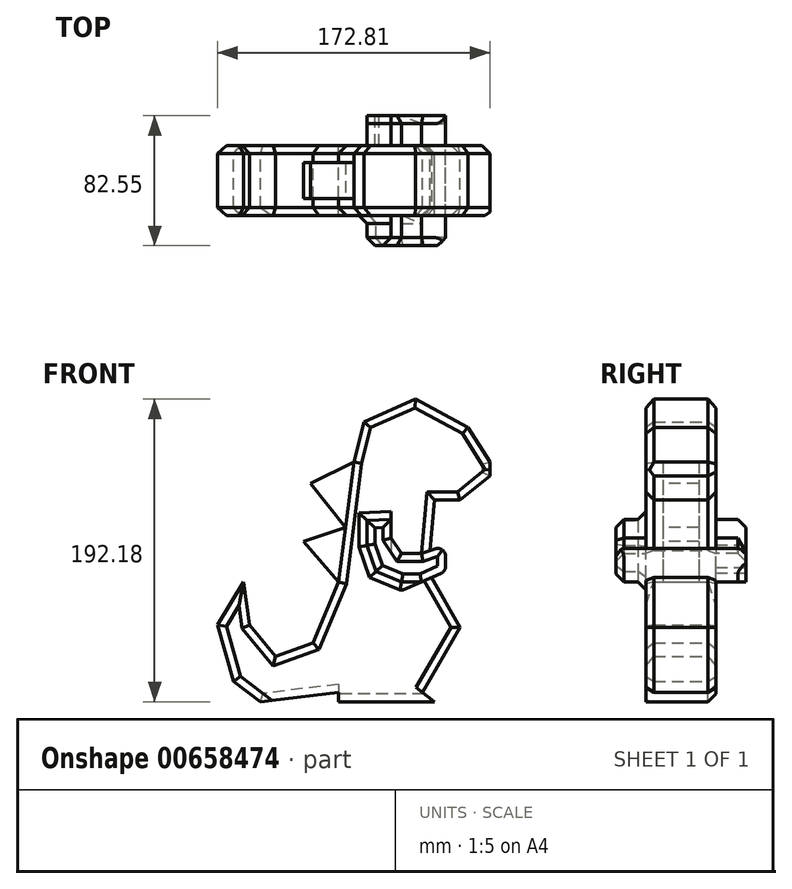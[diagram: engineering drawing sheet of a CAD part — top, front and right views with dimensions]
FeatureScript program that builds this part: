
annotation { "Feature Type Name" : "Feature", "Feature Type Description" : "" }
export const myFeature = defineFeature(function(context is Context, id is Id, definition is map)
    precondition{}
    {
        {
            var Q0;
            Q0=qCreatedBy(makeId("Front.planeOp"),FACE);
            var sketch = newSketch(context, id + "F0", { "sketchPlane" : qUnion([Q0])});
            skLineSegment(sketch, "E0", {"start": v(77.08, 51.94) * mm, "end": v(77.08, 55.91) * mm});
            skLineSegment(sketch, "E1", {"start": v(-60.47, 0) * mm, "end": v(-76.86, -27.51) * mm});
            skLineSegment(sketch, "E2", {"start": v(-76.86, -27.51) * mm, "end": v(-66.68, -63.13) * mm});
            skLineSegment(sketch, "E3", {"start": v(-60.47, 0) * mm, "end": v(-56.5, -27.51) * mm});
            skLineSegment(sketch, "E4", {"start": v(-56.5, -27.51) * mm, "end": v(-40.11, -47.38) * mm});
            skLineSegment(sketch, "E5", {"start": v(-40.11, -47.38) * mm, "end": v(-16.28, -38.93) * mm});
            skLineSegment(sketch, "E6", {"start": v(-16.28, -38.93) * mm, "end": v(0, 0) * mm});
            skPoint(sketch, "E7.start.orphan", {"position": v(68.14, 60.88) * mm});
            skPoint(sketch, "E8.end.orphan", {"position": v(45.3, 0) * mm});
            skPoint(sketch, "E8.start.orphan", {"position": v(68.14, 10.23) * mm});
            skPoint(sketch, "E9.end.orphan", {"position": v(38.54, 76.27) * mm});
            skLineSegment(sketch, "E10", {"start": v(0, 0) * mm, "end": v(9.55, 76.27) * mm});
            skLineSegment(sketch, "E11", {"start": v(-49.55, -76.18) * mm, "end": v(-66.68, -63.13) * mm});
            skLineSegment(sketch, "E12", {"start": v(-49.55, -76.18) * mm, "end": v(0, -70.22) * mm});
            skLineSegment(sketch, "E13", {"start": v(0, -70.22) * mm, "end": v(0, -76.18) * mm});
            skLineSegment(sketch, "E14", {"start": v(0, -76.18) * mm, "end": v(60.7, -76.18) * mm});
            skLineSegment(sketch, "E15", {"start": v(60.7, -76.18) * mm, "end": v(53.24, -70.22) * mm});
            skLineSegment(sketch, "E16", {"start": v(53.24, -70.22) * mm, "end": v(77.08, -29) * mm});
            skLineSegment(sketch, "E17", {"start": v(77.08, -29) * mm, "end": v(56.72, 6.75) * mm});
            skLineSegment(sketch, "E18", {"start": v(56.72, 6.75) * mm, "end": v(60.7, 51.94) * mm});
            skLineSegment(sketch, "E19", {"start": v(60.7, 51.94) * mm, "end": v(77.08, 51.94) * mm});
            skPoint(sketch, "E19.endSnap0", {"position": v(77.08, 55.91) * mm});
            skLineSegment(sketch, "E20", {"start": v(77.08, 51.94) * mm, "end": v(95.95, 67.33) * mm});
            skLineSegment(sketch, "E21", {"start": v(95.95, 67.33) * mm, "end": v(95.95, 76.27) * mm});
            skLineSegment(sketch, "E22", {"start": v(95.95, 76.27) * mm, "end": v(82.05, 98.12) * mm});
            skLineSegment(sketch, "E23", {"start": v(82.05, 98.12) * mm, "end": v(48.78, 116) * mm});
            skLineSegment(sketch, "E24", {"start": v(48.78, 116) * mm, "end": v(16, 101.6) * mm});
            skLineSegment(sketch, "E25", {"start": v(16, 101.6) * mm, "end": v(9.55, 76.27) * mm});
            skPoint(sketch, "E26.orphan", {"position": v(77.08, 76.27) * mm});
            skPoint(sketch, "E27.orphan", {"position": v(77.08, 35.55) * mm});
            skPoint(sketch, "E28.end.orphan", {"position": v(0, 76.27) * mm});
            skSolve(sketch);
        }
        {
            var Q0;
            Q0=makeQuery(id+"F0.imprint","IMPRINT",FACE,{"disambiguationData":[TD([[makeQuery(id+"F0.imprint","IMPRINT",EDGE,{"derivedFrom":sQuery(id+"F0.wireOp",EDGE,"E1")}),1.0]])]});
            extrude(context, id + "F1", {"entities" : qUnion([Q0]), "depth" : 44.45 * mm, "offsetDistance" : 25.4 * mm});
        }
        {
            var Q0;
            Q0=makeQuery(id+"F1.opExtrude","CAP_EDGE",EDGE,{"disambiguationData":[OSD([sQuery(id+"F0.wireOp",EDGE,"E24")])],"isStart":false});
            var Q1;
            Q1=makeQuery(id+"F1.opExtrude","CAP_EDGE",EDGE,{"disambiguationData":[OSD([sQuery(id+"F0.wireOp",EDGE,"E23")])],"isStart":false});
            var Q2;
            Q2=makeQuery(id+"F1.opExtrude","CAP_EDGE",EDGE,{"disambiguationData":[OSD([sQuery(id+"F0.wireOp",EDGE,"E22")])],"isStart":false});
            var Q3;
            Q3=makeQuery(id+"F1.opExtrude","CAP_EDGE",EDGE,{"disambiguationData":[OSD([sQuery(id+"F0.wireOp",EDGE,"E20")])],"isStart":false});
            var Q4;
            Q4=makeQuery(id+"F1.opExtrude","CAP_EDGE",EDGE,{"disambiguationData":[OSD([sQuery(id+"F0.wireOp",EDGE,"E19")])],"isStart":false});
            var Q5;
            Q5=makeQuery(id+"F1.opExtrude","CAP_EDGE",EDGE,{"disambiguationData":[OSD([sQuery(id+"F0.wireOp",EDGE,"E18")])],"isStart":false});
            var Q6;
            Q6=makeQuery(id+"F1.opExtrude","CAP_EDGE",EDGE,{"disambiguationData":[OSD([sQuery(id+"F0.wireOp",EDGE,"E17")])],"isStart":false});
            var Q7;
            Q7=makeQuery(id+"F1.opExtrude","CAP_EDGE",EDGE,{"disambiguationData":[OSD([sQuery(id+"F0.wireOp",EDGE,"E16")])],"isStart":false});
            var Q8;
            Q8=makeQuery(id+"F1.opExtrude","CAP_EDGE",EDGE,{"disambiguationData":[OSD([sQuery(id+"F0.wireOp",EDGE,"E10")])],"isStart":false});
            var Q9;
            Q9=makeQuery(id+"F1.opExtrude","CAP_EDGE",EDGE,{"disambiguationData":[OSD([sQuery(id+"F0.wireOp",EDGE,"E6")])],"isStart":false});
            var Q10;
            Q10=makeQuery(id+"F1.opExtrude","CAP_EDGE",EDGE,{"disambiguationData":[OSD([sQuery(id+"F0.wireOp",EDGE,"E25")])],"isStart":false});
            var Q11;
            Q11=makeQuery(id+"F1.opExtrude","CAP_EDGE",EDGE,{"disambiguationData":[OSD([sQuery(id+"F0.wireOp",EDGE,"E5")])],"isStart":false});
            var Q12;
            Q12=makeQuery(id+"F1.opExtrude","CAP_EDGE",EDGE,{"disambiguationData":[OSD([sQuery(id+"F0.wireOp",EDGE,"E4")])],"isStart":false});
            var Q13;
            Q13=makeQuery(id+"F1.opExtrude","CAP_EDGE",EDGE,{"disambiguationData":[OSD([sQuery(id+"F0.wireOp",EDGE,"E3")])],"isStart":false});
            var Q14;
            Q14=makeQuery(id+"F1.opExtrude","CAP_EDGE",EDGE,{"disambiguationData":[OSD([sQuery(id+"F0.wireOp",EDGE,"E1")])],"isStart":false});
            var Q15;
            Q15=makeQuery(id+"F1.opExtrude","CAP_EDGE",EDGE,{"disambiguationData":[OSD([sQuery(id+"F0.wireOp",EDGE,"E2")])],"isStart":false});
            var Q16;
            Q16=makeQuery(id+"F1.opExtrude","CAP_EDGE",EDGE,{"disambiguationData":[OSD([sQuery(id+"F0.wireOp",EDGE,"E11")])],"isStart":false});
            var Q17;
            Q17=makeQuery(id+"F1.opExtrude","CAP_EDGE",EDGE,{"disambiguationData":[OSD([sQuery(id+"F0.wireOp",EDGE,"E24")])],"isStart":true});
            var Q18;
            Q18=makeQuery(id+"F1.opExtrude","CAP_EDGE",EDGE,{"disambiguationData":[OSD([sQuery(id+"F0.wireOp",EDGE,"E23")])],"isStart":true});
            var Q19;
            Q19=makeQuery(id+"F1.opExtrude","CAP_EDGE",EDGE,{"disambiguationData":[OSD([sQuery(id+"F0.wireOp",EDGE,"E22")])],"isStart":true});
            var Q20;
            Q20=makeQuery(id+"F1.opExtrude","CAP_EDGE",EDGE,{"disambiguationData":[OSD([sQuery(id+"F0.wireOp",EDGE,"E21")])],"isStart":true});
            var Q21;
            Q21=makeQuery(id+"F1.opExtrude","CAP_EDGE",EDGE,{"disambiguationData":[OSD([sQuery(id+"F0.wireOp",EDGE,"E20")])],"isStart":true});
            var Q22;
            Q22=makeQuery(id+"F1.opExtrude","CAP_EDGE",EDGE,{"disambiguationData":[OSD([sQuery(id+"F0.wireOp",EDGE,"E19")])],"isStart":true});
            var Q23;
            Q23=makeQuery(id+"F1.opExtrude","CAP_EDGE",EDGE,{"disambiguationData":[OSD([sQuery(id+"F0.wireOp",EDGE,"E18")])],"isStart":true});
            var Q24;
            Q24=makeQuery(id+"F1.opExtrude","CAP_EDGE",EDGE,{"disambiguationData":[OSD([sQuery(id+"F0.wireOp",EDGE,"E17")])],"isStart":true});
            var Q25;
            Q25=makeQuery(id+"F1.opExtrude","CAP_EDGE",EDGE,{"disambiguationData":[OSD([sQuery(id+"F0.wireOp",EDGE,"E16")])],"isStart":true});
            var Q26;
            Q26=makeQuery(id+"F1.opExtrude","CAP_EDGE",EDGE,{"disambiguationData":[OSD([sQuery(id+"F0.wireOp",EDGE,"E14")])],"isStart":true});
            var Q27;
            Q27=makeQuery(id+"F1.opExtrude","CAP_EDGE",EDGE,{"disambiguationData":[OSD([sQuery(id+"F0.wireOp",EDGE,"E25")])],"isStart":true});
            var Q28;
            Q28=makeQuery(id+"F1.opExtrude","CAP_EDGE",EDGE,{"disambiguationData":[OSD([sQuery(id+"F0.wireOp",EDGE,"E10")])],"isStart":true});
            var Q29;
            Q29=makeQuery(id+"F1.opExtrude","CAP_EDGE",EDGE,{"disambiguationData":[OSD([sQuery(id+"F0.wireOp",EDGE,"E6")])],"isStart":true});
            var Q30;
            Q30=makeQuery(id+"F1.opExtrude","CAP_EDGE",EDGE,{"disambiguationData":[OSD([sQuery(id+"F0.wireOp",EDGE,"E5")])],"isStart":true});
            var Q31;
            Q31=makeQuery(id+"F1.opExtrude","CAP_EDGE",EDGE,{"disambiguationData":[OSD([sQuery(id+"F0.wireOp",EDGE,"E4")])],"isStart":true});
            var Q32;
            Q32=makeQuery(id+"F1.opExtrude","CAP_EDGE",EDGE,{"disambiguationData":[OSD([sQuery(id+"F0.wireOp",EDGE,"E3")])],"isStart":true});
            var Q33;
            Q33=makeQuery(id+"F1.opExtrude","CAP_EDGE",EDGE,{"disambiguationData":[OSD([sQuery(id+"F0.wireOp",EDGE,"E1")])],"isStart":true});
            var Q34;
            Q34=makeQuery(id+"F1.opExtrude","CAP_EDGE",EDGE,{"disambiguationData":[OSD([sQuery(id+"F0.wireOp",EDGE,"E2")])],"isStart":true});
            var Q35;
            Q35=makeQuery(id+"F1.opExtrude","CAP_EDGE",EDGE,{"disambiguationData":[OSD([sQuery(id+"F0.wireOp",EDGE,"E11")])],"isStart":true});
            var Q36;
            Q36=makeQuery(id+"F1.opExtrude","CAP_EDGE",EDGE,{"disambiguationData":[OSD([sQuery(id+"F0.wireOp",EDGE,"E12")])],"isStart":true});
            chamfer(context, id + "F2", {"entities" : qUnion([Q0, Q1, Q2, Q3, Q4, Q5, Q6, Q7, Q8, Q9, Q10, Q11, Q12, Q13, Q14, Q15, Q16, Q17, Q18, Q19, Q20, Q21, Q22, Q23, Q24, Q25, Q26, Q27, Q28, Q29, Q30, Q31, Q32, Q33, Q34, Q35, Q36]), "width" : 5.08 * mm, "tangentPropagation" : true});
        }
        {
            var Q0;
            Q0=makeQuery(id+"F1.opExtrude","CAP_FACE",FACE,{"disambiguationData":[OSD([sQuery(id+"F0.wireOp",EDGE,"E1"),sQuery(id+"F0.wireOp",EDGE,"E2"),sQuery(id+"F0.wireOp",EDGE,"E3"),sQuery(id+"F0.wireOp",EDGE,"E4"),sQuery(id+"F0.wireOp",EDGE,"E5"),sQuery(id+"F0.wireOp",EDGE,"E6"),sQuery(id+"F0.wireOp",EDGE,"E10"),sQuery(id+"F0.wireOp",EDGE,"E11"),sQuery(id+"F0.wireOp",EDGE,"E12"),sQuery(id+"F0.wireOp",EDGE,"E13"),sQuery(id+"F0.wireOp",EDGE,"E14"),sQuery(id+"F0.wireOp",EDGE,"E15"),sQuery(id+"F0.wireOp",EDGE,"E16"),sQuery(id+"F0.wireOp",EDGE,"E17"),sQuery(id+"F0.wireOp",EDGE,"E18"),sQuery(id+"F0.wireOp",EDGE,"E19"),sQuery(id+"F0.wireOp",EDGE,"E20"),sQuery(id+"F0.wireOp",EDGE,"E21"),sQuery(id+"F0.wireOp",EDGE,"E22"),sQuery(id+"F0.wireOp",EDGE,"E23"),sQuery(id+"F0.wireOp",EDGE,"E24"),sQuery(id+"F0.wireOp",EDGE,"E25")])],"isStart":true});
            var sketch = newSketch(context, id + "F3", { "sketchPlane" : qUnion([Q0])});
            skLineSegment(sketch, "E29", {"start": v(-33.23, 39.73) * mm, "end": v(-33.23, 27.8) * mm});
            skLineSegment(sketch, "E30", {"start": v(-33.23, 27.8) * mm, "end": v(-39.78, 18.16) * mm});
            skLineSegment(sketch, "E31", {"start": v(-39.78, 18.16) * mm, "end": v(-52.62, 18.16) * mm});
            skLineSegment(sketch, "E32", {"start": v(-52.62, 18.16) * mm, "end": v(-67.9, 23.17) * mm});
            skLineSegment(sketch, "E33", {"start": v(-67.9, 23.17) * mm, "end": v(-67.9, 6.61) * mm});
            skLineSegment(sketch, "E34", {"start": v(-67.9, 6.61) * mm, "end": v(-52.62, 0) * mm});
            skLineSegment(sketch, "E35", {"start": v(-52.62, 0) * mm, "end": v(-39.78, 0) * mm});
            skLineSegment(sketch, "E36", {"start": v(-39.78, 0) * mm, "end": v(-23.6, 6.61) * mm});
            skLineSegment(sketch, "E37", {"start": v(-23.6, 6.61) * mm, "end": v(-17.83, 23.17) * mm});
            skLineSegment(sketch, "E38", {"start": v(-17.83, 23.17) * mm, "end": v(-17.83, 38.96) * mm});
            skLineSegment(sketch, "E39", {"start": v(-17.83, 38.96) * mm, "end": v(-33.23, 39.73) * mm});
            skSolve(sketch);
        }
        {
            var Q0;
            {var subQ9=sQuery(id+"F3.wireOp",EDGE,"E32");Q0=makeQuery(id+"F3.imprint","IMPRINT",FACE,{"disambiguationData":[TD([[makeQuery(id+"F3.imprint","IMPRINT",EDGE,{"derivedFrom":subQ9}),1.0]])]});}
            var Q1;
            Q1=makeQuery(id+"F3.imprint","IMPRINT",FACE,{"disambiguationData":[TD([[makeQuery(id+"F3.imprint","IMPRINT",EDGE,{"derivedFrom":sQuery(id+"F3.wireOp",EDGE,"E29")}),1.0]])]});
            extrude(context, id + "F4", {"entities" : qUnion([Q0, Q1]), "operationType" : NewBodyOperationType.ADD, "oppositeDirection" : true, "depth" : 63.5 * mm, "offsetDistance" : 25.4 * mm});
        }
        {
            var Q0;
            Q0 = qSketchRegion(id + "F3", true);
            extrude(context, id + "F5", {"entities" : qUnion([Q0]), "operationType" : NewBodyOperationType.ADD, "depth" : 19.05 * mm, "offsetDistance" : 25.4 * mm});
        }
        {
            var Q0;
            Q0=makeQuery(id+"F5.opExtrude","CAP_EDGE",EDGE,{"disambiguationData":[OSD([sQuery(id+"F3.wireOp",EDGE,"E39")])],"isStart":true});
            var Q1;
            Q1=makeQuery(id+"F5.opExtrude","CAP_EDGE",EDGE,{"disambiguationData":[OSD([sQuery(id+"F3.wireOp",EDGE,"E39")])],"isStart":false});
            var Q2;
            Q2=makeQuery(id+"F5.opExtrude","CAP_EDGE",EDGE,{"disambiguationData":[OSD([sQuery(id+"F3.wireOp",EDGE,"E32")])],"isStart":false});
            var Q3;
            Q3=makeQuery(id+"F5.opExtrude","CAP_EDGE",EDGE,{"disambiguationData":[OSD([sQuery(id+"F3.wireOp",EDGE,"E31")])],"isStart":false});
            var Q4;
            Q4=makeQuery(id+"F5.opExtrude","CAP_EDGE",EDGE,{"disambiguationData":[OSD([sQuery(id+"F3.wireOp",EDGE,"E30")])],"isStart":false});
            var Q5;
            Q5=makeQuery(id+"F5.opExtrude","CAP_EDGE",EDGE,{"disambiguationData":[OSD([sQuery(id+"F3.wireOp",EDGE,"E38")])],"isStart":true});
            var Q6;
            Q6=makeQuery(id+"F5.opExtrude","CAP_EDGE",EDGE,{"disambiguationData":[OSD([sQuery(id+"F3.wireOp",EDGE,"E37")])],"isStart":true});
            var Q7;
            Q7=makeQuery(id+"F5.opExtrude","SWEPT_EDGE",EDGE,{"disambiguationData":[OSD([sQuery(id+"F3.wireOp",EDGE,"E36"),sQuery(id+"F3.wireOp",EDGE,"E37")])]});
            var Q8;
            Q8=makeQuery(id+"F5.opExtrude","CAP_EDGE",EDGE,{"disambiguationData":[OSD([sQuery(id+"F3.wireOp",EDGE,"E35")])],"isStart":true});
            var Q9;
            Q9=makeQuery(id+"F5.opExtrude","CAP_EDGE",EDGE,{"disambiguationData":[OSD([sQuery(id+"F3.wireOp",EDGE,"E34")])],"isStart":false});
            var Q10;
            Q10=makeQuery(id+"F4.boolean.opBoolean","INTERSECT",EDGE,{"derivedFrom":[makeQuery(id+"F1.opExtrude","CAP_FACE",FACE,{"disambiguationData":[OSD([sQuery(id+"F0.wireOp",EDGE,"E1"),sQuery(id+"F0.wireOp",EDGE,"E2"),sQuery(id+"F0.wireOp",EDGE,"E3"),sQuery(id+"F0.wireOp",EDGE,"E4"),sQuery(id+"F0.wireOp",EDGE,"E5"),sQuery(id+"F0.wireOp",EDGE,"E6"),sQuery(id+"F0.wireOp",EDGE,"E10"),sQuery(id+"F0.wireOp",EDGE,"E11"),sQuery(id+"F0.wireOp",EDGE,"E12"),sQuery(id+"F0.wireOp",EDGE,"E13"),sQuery(id+"F0.wireOp",EDGE,"E14"),sQuery(id+"F0.wireOp",EDGE,"E15"),sQuery(id+"F0.wireOp",EDGE,"E16"),sQuery(id+"F0.wireOp",EDGE,"E17"),sQuery(id+"F0.wireOp",EDGE,"E18"),sQuery(id+"F0.wireOp",EDGE,"E19"),sQuery(id+"F0.wireOp",EDGE,"E20"),sQuery(id+"F0.wireOp",EDGE,"E21"),sQuery(id+"F0.wireOp",EDGE,"E22"),sQuery(id+"F0.wireOp",EDGE,"E23"),sQuery(id+"F0.wireOp",EDGE,"E24"),sQuery(id+"F0.wireOp",EDGE,"E25")])],"isStart":false}),makeQuery(id+"F4.opExtrude","SWEPT_FACE",FACE,{"disambiguationData":[OSD([sQuery(id+"F3.wireOp",EDGE,"E39")])]})]});
            var Q11;
            Q11=makeQuery(id+"F4.opExtrude","CAP_EDGE",EDGE,{"disambiguationData":[OSD([sQuery(id+"F3.wireOp",EDGE,"E39")])],"isStart":false});
            var Q12;
            Q12=makeQuery(id+"F4.opExtrude","CAP_EDGE",EDGE,{"disambiguationData":[OSD([sQuery(id+"F3.wireOp",EDGE,"E29")])],"isStart":false});
            var Q13;
            Q13=makeQuery(id+"F4.opExtrude","CAP_EDGE",EDGE,{"disambiguationData":[OSD([sQuery(id+"F3.wireOp",EDGE,"E30")])],"isStart":false});
            var Q14;
            Q14=makeQuery(id+"F4.opExtrude","CAP_EDGE",EDGE,{"disambiguationData":[OSD([sQuery(id+"F3.wireOp",EDGE,"E31")])],"isStart":false});
            var Q15;
            Q15=makeQuery(id+"F4.opExtrude","CAP_EDGE",EDGE,{"disambiguationData":[OSD([sQuery(id+"F3.wireOp",EDGE,"E32")])],"isStart":false});
            var Q16;
            Q16=makeQuery(id+"F4.boolean.opBoolean","INTERSECT",EDGE,{"derivedFrom":[makeQuery(id+"F1.opExtrude","CAP_FACE",FACE,{"disambiguationData":[OSD([sQuery(id+"F0.wireOp",EDGE,"E1"),sQuery(id+"F0.wireOp",EDGE,"E2"),sQuery(id+"F0.wireOp",EDGE,"E3"),sQuery(id+"F0.wireOp",EDGE,"E4"),sQuery(id+"F0.wireOp",EDGE,"E5"),sQuery(id+"F0.wireOp",EDGE,"E6"),sQuery(id+"F0.wireOp",EDGE,"E10"),sQuery(id+"F0.wireOp",EDGE,"E11"),sQuery(id+"F0.wireOp",EDGE,"E12"),sQuery(id+"F0.wireOp",EDGE,"E13"),sQuery(id+"F0.wireOp",EDGE,"E14"),sQuery(id+"F0.wireOp",EDGE,"E15"),sQuery(id+"F0.wireOp",EDGE,"E16"),sQuery(id+"F0.wireOp",EDGE,"E17"),sQuery(id+"F0.wireOp",EDGE,"E18"),sQuery(id+"F0.wireOp",EDGE,"E19"),sQuery(id+"F0.wireOp",EDGE,"E20"),sQuery(id+"F0.wireOp",EDGE,"E21"),sQuery(id+"F0.wireOp",EDGE,"E22"),sQuery(id+"F0.wireOp",EDGE,"E23"),sQuery(id+"F0.wireOp",EDGE,"E24"),sQuery(id+"F0.wireOp",EDGE,"E25")])],"isStart":false}),makeQuery(id+"F4.opExtrude","SWEPT_FACE",FACE,{"disambiguationData":[OSD([sQuery(id+"F3.wireOp",EDGE,"E35")])]})]});
            var Q17;
            Q17=makeQuery(id+"F4.boolean.opBoolean","INTERSECT",EDGE,{"derivedFrom":[makeQuery(id+"F1.opExtrude","CAP_FACE",FACE,{"disambiguationData":[OSD([sQuery(id+"F0.wireOp",EDGE,"E1"),sQuery(id+"F0.wireOp",EDGE,"E2"),sQuery(id+"F0.wireOp",EDGE,"E3"),sQuery(id+"F0.wireOp",EDGE,"E4"),sQuery(id+"F0.wireOp",EDGE,"E5"),sQuery(id+"F0.wireOp",EDGE,"E6"),sQuery(id+"F0.wireOp",EDGE,"E10"),sQuery(id+"F0.wireOp",EDGE,"E11"),sQuery(id+"F0.wireOp",EDGE,"E12"),sQuery(id+"F0.wireOp",EDGE,"E13"),sQuery(id+"F0.wireOp",EDGE,"E14"),sQuery(id+"F0.wireOp",EDGE,"E15"),sQuery(id+"F0.wireOp",EDGE,"E16"),sQuery(id+"F0.wireOp",EDGE,"E17"),sQuery(id+"F0.wireOp",EDGE,"E18"),sQuery(id+"F0.wireOp",EDGE,"E19"),sQuery(id+"F0.wireOp",EDGE,"E20"),sQuery(id+"F0.wireOp",EDGE,"E21"),sQuery(id+"F0.wireOp",EDGE,"E22"),sQuery(id+"F0.wireOp",EDGE,"E23"),sQuery(id+"F0.wireOp",EDGE,"E24"),sQuery(id+"F0.wireOp",EDGE,"E25")])],"isStart":false}),makeQuery(id+"F4.opExtrude","SWEPT_FACE",FACE,{"disambiguationData":[OSD([sQuery(id+"F3.wireOp",EDGE,"E36")])]})]});
            var Q18;
            Q18=makeQuery(id+"F4.boolean.opBoolean","INTERSECT",EDGE,{"derivedFrom":[makeQuery(id+"F1.opExtrude","CAP_FACE",FACE,{"disambiguationData":[OSD([sQuery(id+"F0.wireOp",EDGE,"E1"),sQuery(id+"F0.wireOp",EDGE,"E2"),sQuery(id+"F0.wireOp",EDGE,"E3"),sQuery(id+"F0.wireOp",EDGE,"E4"),sQuery(id+"F0.wireOp",EDGE,"E5"),sQuery(id+"F0.wireOp",EDGE,"E6"),sQuery(id+"F0.wireOp",EDGE,"E10"),sQuery(id+"F0.wireOp",EDGE,"E11"),sQuery(id+"F0.wireOp",EDGE,"E12"),sQuery(id+"F0.wireOp",EDGE,"E13"),sQuery(id+"F0.wireOp",EDGE,"E14"),sQuery(id+"F0.wireOp",EDGE,"E15"),sQuery(id+"F0.wireOp",EDGE,"E16"),sQuery(id+"F0.wireOp",EDGE,"E17"),sQuery(id+"F0.wireOp",EDGE,"E18"),sQuery(id+"F0.wireOp",EDGE,"E19"),sQuery(id+"F0.wireOp",EDGE,"E20"),sQuery(id+"F0.wireOp",EDGE,"E21"),sQuery(id+"F0.wireOp",EDGE,"E22"),sQuery(id+"F0.wireOp",EDGE,"E23"),sQuery(id+"F0.wireOp",EDGE,"E24"),sQuery(id+"F0.wireOp",EDGE,"E25")])],"isStart":false}),makeQuery(id+"F4.opExtrude","SWEPT_FACE",FACE,{"disambiguationData":[OSD([sQuery(id+"F3.wireOp",EDGE,"E38")])]})]});
            var Q19;
            Q19=makeQuery(id+"F4.boolean.opBoolean","INTERSECT",EDGE,{"derivedFrom":[makeQuery(id+"F1.opExtrude","CAP_FACE",FACE,{"disambiguationData":[OSD([sQuery(id+"F0.wireOp",EDGE,"E1"),sQuery(id+"F0.wireOp",EDGE,"E2"),sQuery(id+"F0.wireOp",EDGE,"E3"),sQuery(id+"F0.wireOp",EDGE,"E4"),sQuery(id+"F0.wireOp",EDGE,"E5"),sQuery(id+"F0.wireOp",EDGE,"E6"),sQuery(id+"F0.wireOp",EDGE,"E10"),sQuery(id+"F0.wireOp",EDGE,"E11"),sQuery(id+"F0.wireOp",EDGE,"E12"),sQuery(id+"F0.wireOp",EDGE,"E13"),sQuery(id+"F0.wireOp",EDGE,"E14"),sQuery(id+"F0.wireOp",EDGE,"E15"),sQuery(id+"F0.wireOp",EDGE,"E16"),sQuery(id+"F0.wireOp",EDGE,"E17"),sQuery(id+"F0.wireOp",EDGE,"E18"),sQuery(id+"F0.wireOp",EDGE,"E19"),sQuery(id+"F0.wireOp",EDGE,"E20"),sQuery(id+"F0.wireOp",EDGE,"E21"),sQuery(id+"F0.wireOp",EDGE,"E22"),sQuery(id+"F0.wireOp",EDGE,"E23"),sQuery(id+"F0.wireOp",EDGE,"E24"),sQuery(id+"F0.wireOp",EDGE,"E25")])],"isStart":false}),makeQuery(id+"F4.opExtrude","SWEPT_FACE",FACE,{"disambiguationData":[OSD([sQuery(id+"F3.wireOp",EDGE,"E37")])]})]});
            chamfer(context, id + "F6", {"entities" : qUnion([Q0, Q1, Q2, Q3, Q4, Q5, Q6, Q7, Q8, Q9, Q10, Q11, Q12, Q13, Q14, Q15, Q16, Q17, Q18, Q19]), "width" : 5.08 * mm, "tangentPropagation" : true});
        }
        {
            var Q0;
            Q0=makeQuery(id+"F1.opExtrude","SWEPT_FACE",FACE,{"disambiguationData":[OSD([sQuery(id+"F0.wireOp",EDGE,"E10")])]});
            var sketch = newSketch(context, id + "F7", { "sketchPlane" : qUnion([Q0])});
            skLineSegment(sketch, "E40.bottom", {"start": v(17.14, 76.86) * mm, "end": v(26.38, 76.86) * mm});
            skLineSegment(sketch, "E40.top", {"start": v(17.14, 0) * mm, "end": v(26.38, 0) * mm});
            skLineSegment(sketch, "E40.left", {"start": v(17.14, 76.86) * mm, "end": v(17.14, 0) * mm});
            skLineSegment(sketch, "E40.right", {"start": v(26.38, 76.86) * mm, "end": v(26.38, 0) * mm});
            skSolve(sketch);
        }
        {
            var Q0;
            Q0 = qSketchRegion(id + "F7", true);
            extrude(context, id + "F8", {"entities" : qUnion([Q0]), "operationType" : NewBodyOperationType.ADD, "depth" : 25.4 * mm, "offsetDistance" : 25.4 * mm});
        }
        {
            var Q0;
            Q0=makeQuery(id+"F8.opExtrude","SWEPT_FACE",FACE,{"disambiguationData":[OSD([sQuery(id+"F7.wireOp",EDGE,"E40.left")])]});
            var sketch = newSketch(context, id + "F9", { "sketchPlane" : qUnion([Q0])});
            skLineSegment(sketch, "E41", {"start": v(-9.55, 76.27) * mm, "end": v(17.76, 62.62) * mm});
            skLineSegment(sketch, "E42", {"start": v(17.76, 62.62) * mm, "end": v(-4.33, 34.58) * mm});
            skLineSegment(sketch, "E43", {"start": v(-4.33, 34.58) * mm, "end": v(22.4, 25.6) * mm});
            skLineSegment(sketch, "E44", {"start": v(22.4, 25.6) * mm, "end": v(0, 0) * mm});
            skSolve(sketch);
        }
        {
            var Q0;
            {var subQ0=sQuery(id+"F9.wireOp",EDGE,"E41");Q0=makeQuery(id+"F9.imprint","IMPRINT",FACE,{"disambiguationData":[TD([[makeQuery(id+"F9.imprint","IMPRINT",EDGE,{"derivedFrom":subQ0}),-1.0]])]});}
            var Q1;
            {var subQ0=sQuery(id+"F9.wireOp",EDGE,"E43");Q1=makeQuery(id+"F9.imprint","IMPRINT",FACE,{"disambiguationData":[TD([[makeQuery(id+"F9.imprint","IMPRINT",EDGE,{"derivedFrom":subQ0}),-1.0]])]});}
            extrude(context, id + "F10", {"entities" : qUnion([Q0, Q1]), "operationType" : NewBodyOperationType.ADD, "depth" : 6.35 * mm, "offsetDistance" : 25.4 * mm});
        }
        {
            var Q0;
            Q0=makeQuery(id+"F10.opExtrude","CAP_FACE",FACE,{"disambiguationData":[OSD([sQuery(id+"F7.wireOp",EDGE,"E40.left"),sQuery(id+"F9.wireOp",EDGE,"E41"),sQuery(id+"F9.wireOp",EDGE,"E42")])],"isStart":false});
            var Q1;
            Q1=makeQuery(id+"F10.opExtrude","CAP_FACE",FACE,{"disambiguationData":[OSD([sQuery(id+"F7.wireOp",EDGE,"E40.left"),sQuery(id+"F9.wireOp",EDGE,"E43"),sQuery(id+"F9.wireOp",EDGE,"E44")])],"isStart":false});
            extrude(context, id + "F11", {"entities" : qUnion([Q0, Q1]), "operationType" : NewBodyOperationType.ADD, "oppositeDirection" : true, "depth" : 22.6 * mm, "offsetDistance" : 25.4 * mm});
        }
        {
            var Q0;
            {var subQ0=sQuery(id+"F3.wireOp",EDGE,"E33");var subQ1=sQuery(id+"F3.wireOp",EDGE,"E32");Q0=makeQuery(id+"F5.boolean.opBoolean","MERGE",EDGE,{"derivedFrom":[makeQuery(id+"F4.opExtrude","SWEPT_EDGE",EDGE,{"disambiguationData":[OSD([subQ1,subQ0])]}),makeQuery(id+"F5.opExtrude","SWEPT_EDGE",EDGE,{"disambiguationData":[OSD([subQ1,subQ0])]})]});}
            var Q1;
            {var subQ0=sQuery(id+"F3.wireOp",EDGE,"E34");var subQ1=sQuery(id+"F3.wireOp",EDGE,"E33");Q1=makeQuery(id+"F5.boolean.opBoolean","MERGE",EDGE,{"derivedFrom":[makeQuery(id+"F4.opExtrude","SWEPT_EDGE",EDGE,{"disambiguationData":[OSD([subQ1,subQ0])]}),makeQuery(id+"F5.opExtrude","SWEPT_EDGE",EDGE,{"disambiguationData":[OSD([subQ1,subQ0])]})]});}
            fillet(context, id + "F12", {"entities" : qUnion([Q0, Q1]), "radius" : 5.08 * mm, "tangentPropagation" : true, "allowEdgeOverflow" : false});
        }
        {
            var Q0;
            Q0=makeQuery(id+"F4.opExtrude","CAP_EDGE",EDGE,{"disambiguationData":[OSD([sQuery(id+"F3.wireOp",EDGE,"E34")])],"isStart":false});
            var Q1;
            Q1=makeQuery(id+"F4.opExtrude","CAP_EDGE",EDGE,{"disambiguationData":[OSD([sQuery(id+"F3.wireOp",EDGE,"E36")])],"isStart":false});
            var Q2;
            Q2=makeQuery(id+"F4.opExtrude","CAP_EDGE",EDGE,{"disambiguationData":[OSD([sQuery(id+"F3.wireOp",EDGE,"E37")])],"isStart":false});
            var Q3;
            Q3=makeQuery(id+"F4.opExtrude","CAP_EDGE",EDGE,{"disambiguationData":[OSD([sQuery(id+"F3.wireOp",EDGE,"E38")])],"isStart":false});
            var Q4;
            Q4=makeQuery(id+"F4.opExtrude","CAP_EDGE",EDGE,{"disambiguationData":[OSD([sQuery(id+"F3.wireOp",EDGE,"E35")])],"isStart":false});
            chamfer(context, id + "F13", {"entities" : qUnion([Q0, Q1, Q2, Q3, Q4]), "width" : 5.08 * mm, "tangentPropagation" : true});
        }
        {
            var Q0;
            {var subQ0=sQuery(id+"F7.wireOp",EDGE,"E40.right");var subQ1=makeQuery(id+"F8.opExtrude","SWEPT_FACE",FACE,{"disambiguationData":[OSD([subQ0])]});var subQ2=sQuery(id+"F7.wireOp",EDGE,"E40.bottom");Q0=makeQuery(id+"F11.boolean.opBoolean","SPLIT",FACE,{"disambiguationData":[TD([makeQuery(id+"F1.opExtrude","SWEPT_FACE",FACE,{"disambiguationData":[OSD([sQuery(id+"F0.wireOp",EDGE,"E25")])]}),makeQuery(id+"F8.opExtrude","SWEPT_FACE",FACE,{"disambiguationData":[OSD([subQ2])]}),makeQuery(id+"F8.opExtrude","CAP_FACE",FACE,{"disambiguationData":[OSD([subQ2,sQuery(id+"F7.wireOp",EDGE,"E40.top"),sQuery(id+"F7.wireOp",EDGE,"E40.left"),subQ0])],"isStart":false}),subQ1,makeQuery(id+"F11.opExtrude","SWEPT_FACE",FACE,{"disambiguationData":[OSD([sQuery(id+"F9.wireOp",EDGE,"E41")])]}),makeQuery(id+"F11.opExtrude","SWEPT_FACE",FACE,{"disambiguationData":[OSD([sQuery(id+"F9.wireOp",EDGE,"E42")])]})])],"derivedFrom":subQ1});}
            var Q1;
            {var subQ0=sQuery(id+"F7.wireOp",EDGE,"E40.right");var subQ1=makeQuery(id+"F8.opExtrude","SWEPT_FACE",FACE,{"disambiguationData":[OSD([subQ0])]});Q1=makeQuery(id+"F11.boolean.opBoolean","SPLIT",FACE,{"disambiguationData":[TD([makeQuery(id+"F8.opExtrude","CAP_FACE",FACE,{"disambiguationData":[OSD([sQuery(id+"F7.wireOp",EDGE,"E40.bottom"),sQuery(id+"F7.wireOp",EDGE,"E40.top"),sQuery(id+"F7.wireOp",EDGE,"E40.left"),subQ0])],"isStart":false}),subQ1,makeQuery(id+"F11.opExtrude","SWEPT_FACE",FACE,{"disambiguationData":[OSD([sQuery(id+"F9.wireOp",EDGE,"E41")])]}),makeQuery(id+"F11.opExtrude","SWEPT_FACE",FACE,{"disambiguationData":[OSD([sQuery(id+"F9.wireOp",EDGE,"E42")])]}),makeQuery(id+"F11.opExtrude","SWEPT_FACE",FACE,{"disambiguationData":[OSD([sQuery(id+"F9.wireOp",EDGE,"E43")])]}),makeQuery(id+"F11.opExtrude","SWEPT_FACE",FACE,{"disambiguationData":[OSD([sQuery(id+"F9.wireOp",EDGE,"E44")])]})])],"derivedFrom":subQ1});}
            var Q2;
            {var subQ0=sQuery(id+"F7.wireOp",EDGE,"E40.right");var subQ1=makeQuery(id+"F8.opExtrude","SWEPT_FACE",FACE,{"disambiguationData":[OSD([subQ0])]});var subQ2=sQuery(id+"F7.wireOp",EDGE,"E40.top");Q2=makeQuery(id+"F11.boolean.opBoolean","SPLIT",FACE,{"disambiguationData":[TD([makeQuery(id+"F1.opExtrude","SWEPT_FACE",FACE,{"disambiguationData":[OSD([sQuery(id+"F0.wireOp",EDGE,"E6")])]}),makeQuery(id+"F8.opExtrude","CAP_FACE",FACE,{"disambiguationData":[OSD([sQuery(id+"F7.wireOp",EDGE,"E40.bottom"),subQ2,sQuery(id+"F7.wireOp",EDGE,"E40.left"),subQ0])],"isStart":false}),makeQuery(id+"F8.opExtrude","SWEPT_FACE",FACE,{"disambiguationData":[OSD([subQ2])]}),subQ1,makeQuery(id+"F11.opExtrude","SWEPT_FACE",FACE,{"disambiguationData":[OSD([sQuery(id+"F9.wireOp",EDGE,"E43")])]}),makeQuery(id+"F11.opExtrude","SWEPT_FACE",FACE,{"disambiguationData":[OSD([sQuery(id+"F9.wireOp",EDGE,"E44")])]})])],"derivedFrom":subQ1});}
            extrude(context, id + "F14", {"entities" : qUnion([Q0, Q1, Q2]), "operationType" : NewBodyOperationType.REMOVE, "oppositeDirection" : true, "depth" : 50.8 * mm, "offsetDistance" : 25.4 * mm});
        }
    });
